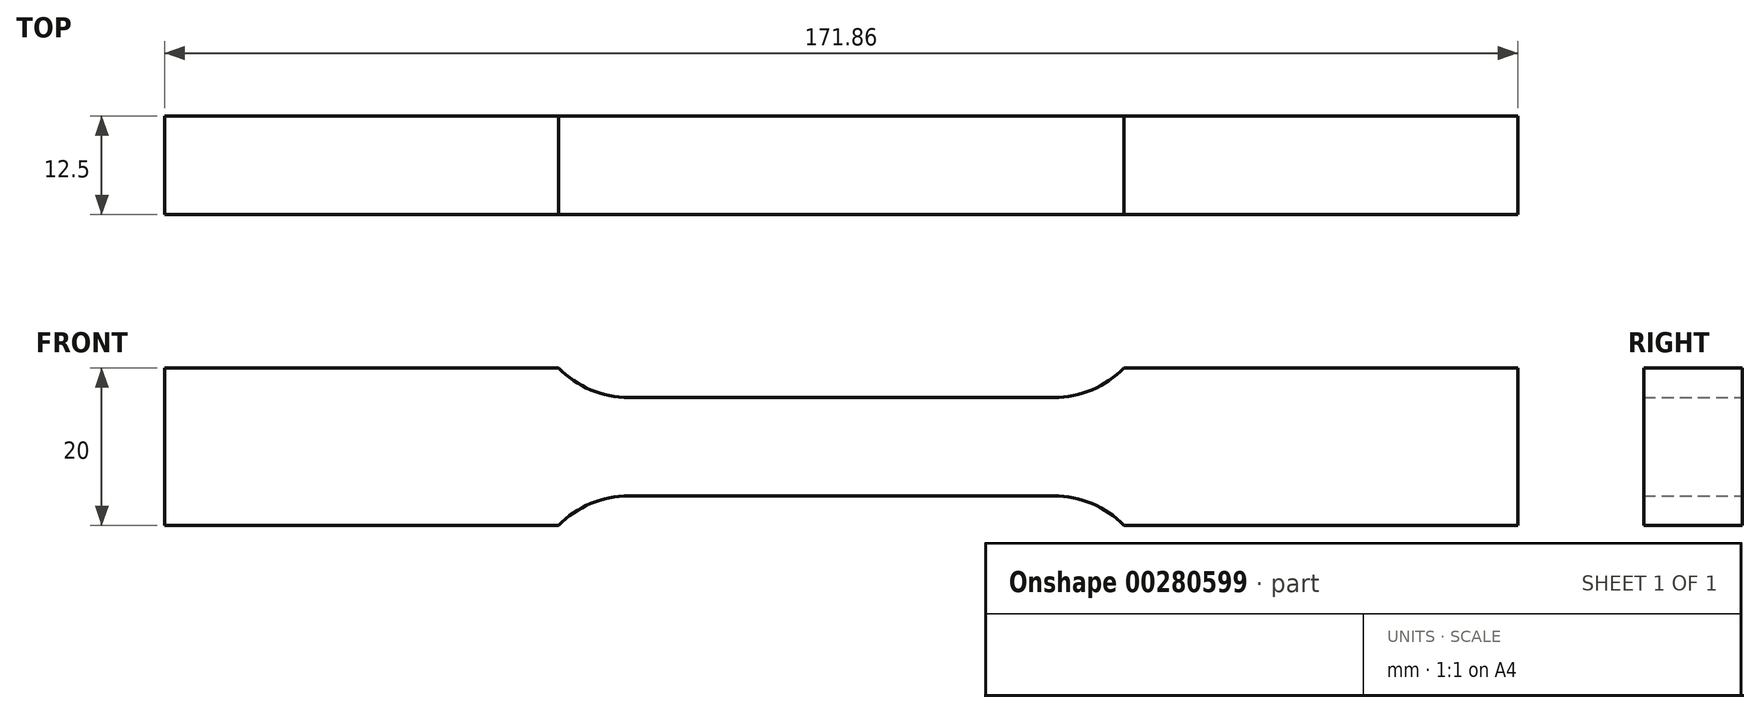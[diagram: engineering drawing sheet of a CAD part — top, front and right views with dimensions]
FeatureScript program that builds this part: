
annotation { "Feature Type Name" : "Feature", "Feature Type Description" : "" }
export const myFeature = defineFeature(function(context is Context, id is Id, definition is map)
    precondition{}
    {
        {
            var Q0;
            Q0=qCreatedBy(makeId("Front.planeOp"),FACE);
            var sketch = newSketch(context, id + "F0", { "sketchPlane" : qUnion([Q0])});
            skLineSegment(sketch, "E0", {"start": v(0, -6.25) * mm, "end": v(27, -6.25) * mm});
            skLineSegment(sketch, "E1", {"start": v(35.93, 10) * mm, "end": v(85.93, 10) * mm});
            skLineSegment(sketch, "E2", {"start": v(85.93, 10) * mm, "end": v(85.93, 0) * mm});
            skLineSegment(sketch, "E3.MirrorCS", {"start": v(85.93, -10) * mm, "end": v(85.93, 0) * mm});
            skLineSegment(sketch, "E4.MirrorCS", {"start": v(35.93, -10) * mm, "end": v(85.93, -10) * mm});
            skLineSegment(sketch, "E5.MirrorCS", {"start": v(0, 6.25) * mm, "end": v(27, 6.25) * mm});
            skArc(sketch, "E6", {"start": v(27, 6.25) * mm, "mid": v(31.84, 7.23) * mm, "end": v(35.93, 10) * mm});
            skArc(sketch, "E7", {"start": v(35.93, -10) * mm, "mid": v(31.84, -7.23) * mm, "end": v(27, -6.25) * mm});
            skLineSegment(sketch, "E8.MirrorCS", {"start": v(0, 6.25) * mm, "end": v(-27, 6.25) * mm});
            skArc(sketch, "E9.MirrorCS", {"start": v(-27, 6.25) * mm, "mid": v(-31.84, 7.23) * mm, "end": v(-35.93, 10) * mm});
            skLineSegment(sketch, "E10.MirrorCS", {"start": v(-85.93, 10) * mm, "end": v(-85.93, 0) * mm});
            skLineSegment(sketch, "E11.MirrorCS", {"start": v(0, -6.25) * mm, "end": v(-27, -6.25) * mm});
            skArc(sketch, "E12.MirrorCS", {"start": v(-35.93, -10) * mm, "mid": v(-31.84, -7.23) * mm, "end": v(-27, -6.25) * mm});
            skLineSegment(sketch, "E13.MirrorCS", {"start": v(-85.93, -10) * mm, "end": v(-85.93, 0) * mm});
            skLineSegment(sketch, "E14.MirrorCS", {"start": v(-35.93, -10) * mm, "end": v(-85.93, -10) * mm});
            skLineSegment(sketch, "E15.MirrorCS", {"start": v(-35.93, 10) * mm, "end": v(-85.93, 10) * mm});
            skSolve(sketch);
        }
        {
            var Q0;
            Q0=makeQuery(id+"F0.imprint","IMPRINT",FACE,{"disambiguationData":[TD([[makeQuery(id+"F0.imprint","IMPRINT",EDGE,{"derivedFrom":sQuery(id+"F0.wireOp",EDGE,"E0")}),1.0]])]});
            extrude(context, id + "F1", {"entities" : qUnion([Q0]), "endBound" : BoundingType.SYMMETRIC, "depth" : 12.5 * mm});
        }
    });
